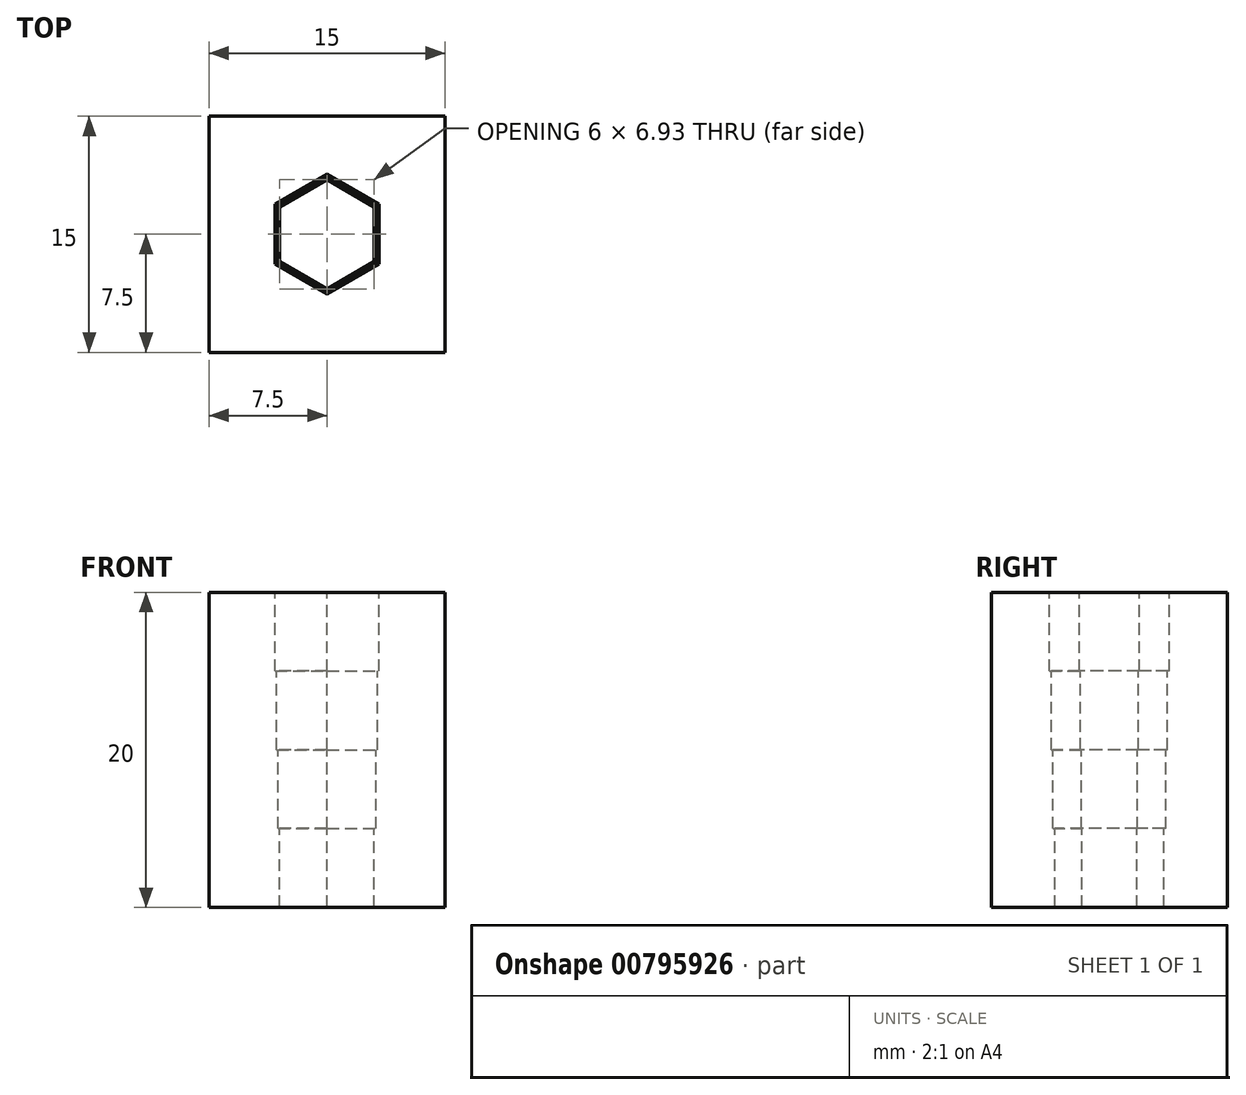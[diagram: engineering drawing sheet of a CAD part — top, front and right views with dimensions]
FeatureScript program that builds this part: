
annotation { "Feature Type Name" : "Feature", "Feature Type Description" : "" }
export const myFeature = defineFeature(function(context is Context, id is Id, definition is map)
    precondition{}
    {
        {
            var Q0;
            Q0=qCreatedBy(makeId("Top.planeOp"),FACE);
            var sketch = newSketch(context, id + "F0", { "sketchPlane" : qUnion([Q0])});
            skLineSegment(sketch, "E0.bottom", {"start": v(7.5, -7.5) * mm, "end": v(-7.5, -7.5) * mm});
            skLineSegment(sketch, "E0.top", {"start": v(7.5, 7.5) * mm, "end": v(-7.5, 7.5) * mm});
            skLineSegment(sketch, "E0.left", {"start": v(7.5, -7.5) * mm, "end": v(7.5, 7.5) * mm});
            skLineSegment(sketch, "E0.right", {"start": v(-7.5, -7.5) * mm, "end": v(-7.5, 7.5) * mm});
            skPoint(sketch, "E0.middle", {"position": v(0, 0) * mm});
            skSolve(sketch);
        }
        {
            var Q0;
            Q0=makeQuery(id+"F0.imprint","IMPRINT",FACE,{"disambiguationData":[TD([[makeQuery(id+"F0.imprint","IMPRINT",EDGE,{"derivedFrom":sQuery(id+"F0.wireOp",EDGE,"E0.bottom")}),-1.0]])]});
            extrude(context, id + "F1", {"entities" : qUnion([Q0]), "depth" : 20 * mm, "offsetDistance" : 25 * mm});
        }
        {
            var Q0;
            Q0=makeQuery(id+"F1.opExtrude","CAP_FACE",FACE,{"disambiguationData":[OSD([sQuery(id+"F0.wireOp",EDGE,"E0.bottom"),sQuery(id+"F0.wireOp",EDGE,"E0.top"),sQuery(id+"F0.wireOp",EDGE,"E0.left"),sQuery(id+"F0.wireOp",EDGE,"E0.right")])],"isStart":false});
            var sketch = newSketch(context, id + "F2", { "sketchPlane" : qUnion([Q0])});
            skCircle(sketch, "E1.cCircle", {"center": v(0, 0) * mm, "radius": 3.3 * mm, "construction": true});
            skLineSegment(sketch, "E1.0", {"start": v(3.3, 1.9) * mm, "end": v(3.3, -1.9) * mm});
            skLineSegment(sketch, "E1.1", {"start": v(3.3, -1.9) * mm, "end": v(0, -3.81) * mm});
            skLineSegment(sketch, "E1.2", {"start": v(0, -3.81) * mm, "end": v(-3.3, -1.9) * mm});
            skLineSegment(sketch, "E1.3", {"start": v(-3.3, -1.9) * mm, "end": v(-3.3, 1.9) * mm});
            skLineSegment(sketch, "E1.4", {"start": v(-3.3, 1.9) * mm, "end": v(0, 3.81) * mm});
            skLineSegment(sketch, "E1.5", {"start": v(0, 3.81) * mm, "end": v(3.3, 1.9) * mm});
            skPoint(sketch, "E1.0.midPoint", {"position": v(3.3, 0) * mm});
            skSolve(sketch);
        }
        {
            var Q0;
            Q0=makeQuery(id+"F2.imprint","IMPRINT",FACE,{"disambiguationData":[TD([[makeQuery(id+"F2.imprint","IMPRINT",EDGE,{"derivedFrom":sQuery(id+"F2.wireOp",EDGE,"E1.0")}),-1.0]])]});
            extrude(context, id + "F3", {"entities" : qUnion([Q0]), "operationType" : NewBodyOperationType.REMOVE, "oppositeDirection" : true, "depth" : 5 * mm, "offsetDistance" : 25 * mm});
        }
        {
            var Q0;
            Q0=makeQuery(id+"F3.boolean.opBoolean","COPY",FACE,{"derivedFrom":makeQuery(id+"F3.opExtrude","CAP_FACE",FACE,{"disambiguationData":[OSD([sQuery(id+"F2.wireOp",EDGE,"E1.0"),sQuery(id+"F2.wireOp",EDGE,"E1.1"),sQuery(id+"F2.wireOp",EDGE,"E1.2"),sQuery(id+"F2.wireOp",EDGE,"E1.3"),sQuery(id+"F2.wireOp",EDGE,"E1.4"),sQuery(id+"F2.wireOp",EDGE,"E1.5")])],"isStart":false})});
            var sketch = newSketch(context, id + "F4", { "sketchPlane" : qUnion([Q0])});
            skCircle(sketch, "E2.cCircle", {"center": v(0, 0) * mm, "radius": 3.2 * mm, "construction": true});
            skLineSegment(sketch, "E2.0", {"start": v(3.2, 1.85) * mm, "end": v(3.2, -1.85) * mm});
            skLineSegment(sketch, "E2.1", {"start": v(3.2, -1.85) * mm, "end": v(0, -3.7) * mm});
            skLineSegment(sketch, "E2.2", {"start": v(0, -3.7) * mm, "end": v(-3.2, -1.85) * mm});
            skLineSegment(sketch, "E2.3", {"start": v(-3.2, -1.85) * mm, "end": v(-3.2, 1.85) * mm});
            skLineSegment(sketch, "E2.4", {"start": v(-3.2, 1.85) * mm, "end": v(0, 3.7) * mm});
            skLineSegment(sketch, "E2.5", {"start": v(0, 3.7) * mm, "end": v(3.2, 1.85) * mm});
            skPoint(sketch, "E2.0.midPoint", {"position": v(3.2, 0) * mm});
            skSolve(sketch);
        }
        {
            var Q0;
            Q0=makeQuery(id+"F4.imprint","IMPRINT",FACE,{"disambiguationData":[TD([[makeQuery(id+"F4.imprint","IMPRINT",EDGE,{"derivedFrom":sQuery(id+"F4.wireOp",EDGE,"E2.0")}),-1.0]])]});
            var Q1;
            Q1 = qSketchRegion(id + "F4", true);
            extrude(context, id + "F5", {"entities" : qUnion([Q0, Q1]), "operationType" : NewBodyOperationType.REMOVE, "oppositeDirection" : true, "depth" : 5 * mm, "offsetDistance" : 25 * mm});
        }
        {
            var Q0;
            Q0=makeQuery(id+"F5.boolean.opBoolean","COPY",FACE,{"derivedFrom":makeQuery(id+"F5.opExtrude","CAP_FACE",FACE,{"disambiguationData":[OSD([sQuery(id+"F4.wireOp",EDGE,"E2.0"),sQuery(id+"F4.wireOp",EDGE,"E2.1"),sQuery(id+"F4.wireOp",EDGE,"E2.2"),sQuery(id+"F4.wireOp",EDGE,"E2.3"),sQuery(id+"F4.wireOp",EDGE,"E2.4"),sQuery(id+"F4.wireOp",EDGE,"E2.5")])],"isStart":false})});
            var sketch = newSketch(context, id + "F6", { "sketchPlane" : qUnion([Q0])});
            skCircle(sketch, "E3.cCircle", {"center": v(0, 0) * mm, "radius": 3.1 * mm, "construction": true});
            skLineSegment(sketch, "E3.0", {"start": v(3.1, 1.79) * mm, "end": v(3.1, -1.79) * mm});
            skLineSegment(sketch, "E3.1", {"start": v(3.1, -1.79) * mm, "end": v(0, -3.58) * mm});
            skLineSegment(sketch, "E3.2", {"start": v(0, -3.58) * mm, "end": v(-3.1, -1.79) * mm});
            skLineSegment(sketch, "E3.3", {"start": v(-3.1, -1.79) * mm, "end": v(-3.1, 1.79) * mm});
            skLineSegment(sketch, "E3.4", {"start": v(-3.1, 1.79) * mm, "end": v(0, 3.58) * mm});
            skLineSegment(sketch, "E3.5", {"start": v(0, 3.58) * mm, "end": v(3.1, 1.79) * mm});
            skPoint(sketch, "E3.0.midPoint", {"position": v(3.1, 0) * mm});
            skSolve(sketch);
        }
        {
            var Q0;
            Q0=makeQuery(id+"F6.imprint","IMPRINT",FACE,{"disambiguationData":[TD([[makeQuery(id+"F6.imprint","IMPRINT",EDGE,{"derivedFrom":sQuery(id+"F6.wireOp",EDGE,"E3.0")}),-1.0]])]});
            extrude(context, id + "F7", {"entities" : qUnion([Q0]), "operationType" : NewBodyOperationType.REMOVE, "oppositeDirection" : true, "depth" : 5 * mm, "offsetDistance" : 25 * mm});
        }
        {
            var Q0;
            Q0=makeQuery(id+"F7.boolean.opBoolean","COPY",FACE,{"derivedFrom":makeQuery(id+"F7.opExtrude","CAP_FACE",FACE,{"disambiguationData":[OSD([sQuery(id+"F6.wireOp",EDGE,"E3.0"),sQuery(id+"F6.wireOp",EDGE,"E3.1"),sQuery(id+"F6.wireOp",EDGE,"E3.2"),sQuery(id+"F6.wireOp",EDGE,"E3.3"),sQuery(id+"F6.wireOp",EDGE,"E3.4"),sQuery(id+"F6.wireOp",EDGE,"E3.5")])],"isStart":false})});
            var sketch = newSketch(context, id + "F8", { "sketchPlane" : qUnion([Q0])});
            skCircle(sketch, "E4.cCircle", {"center": v(0, 0) * mm, "radius": 3 * mm, "construction": true});
            skLineSegment(sketch, "E4.0", {"start": v(3, 1.73) * mm, "end": v(3, -1.73) * mm});
            skLineSegment(sketch, "E4.1", {"start": v(3, -1.73) * mm, "end": v(0, -3.46) * mm});
            skLineSegment(sketch, "E4.2", {"start": v(0, -3.46) * mm, "end": v(-3, -1.73) * mm});
            skLineSegment(sketch, "E4.3", {"start": v(-3, -1.73) * mm, "end": v(-3, 1.73) * mm});
            skLineSegment(sketch, "E4.4", {"start": v(-3, 1.73) * mm, "end": v(0, 3.46) * mm});
            skLineSegment(sketch, "E4.5", {"start": v(0, 3.46) * mm, "end": v(3, 1.73) * mm});
            skPoint(sketch, "E4.0.midPoint", {"position": v(3, 0) * mm});
            skSolve(sketch);
        }
        {
            var Q0;
            Q0=makeQuery(id+"F8.imprint","IMPRINT",FACE,{"disambiguationData":[TD([[makeQuery(id+"F8.imprint","IMPRINT",EDGE,{"derivedFrom":sQuery(id+"F8.wireOp",EDGE,"E4.0")}),-1.0]])]});
            extrude(context, id + "F9", {"entities" : qUnion([Q0]), "operationType" : NewBodyOperationType.REMOVE, "oppositeDirection" : true, "depth" : 5 * mm, "offsetDistance" : 25 * mm});
        }
    });
